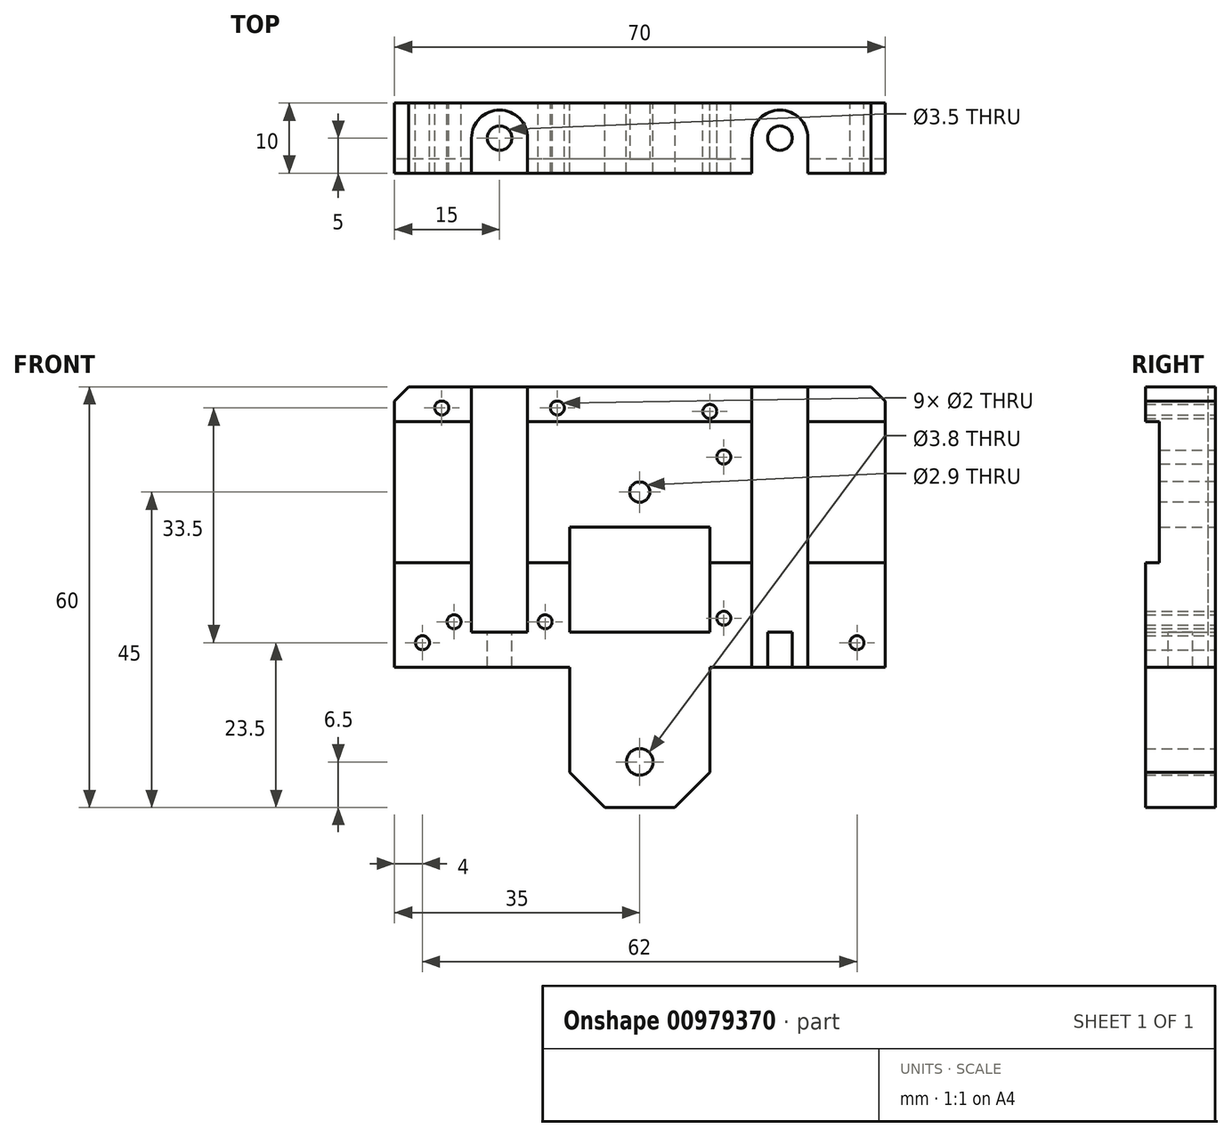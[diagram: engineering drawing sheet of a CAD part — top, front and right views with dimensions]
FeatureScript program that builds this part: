
annotation { "Feature Type Name" : "Feature", "Feature Type Description" : "" }
export const myFeature = defineFeature(function(context is Context, id is Id, definition is map)
    precondition{}
    {
        {
            var Q0;
            Q0=qCreatedBy(makeId("Front.planeOp"),FACE);
            var sketch = newSketch(context, id + "F0", { "sketchPlane" : qUnion([Q0])});
            skLineSegment(sketch, "E0.bottom", {"start": v(-35, 40) * mm, "end": v(35, 40) * mm});
            skLineSegment(sketch, "E0.top", {"start": v(-35, 0) * mm, "end": v(35, 0) * mm});
            skLineSegment(sketch, "E0.left", {"start": v(-35, 40) * mm, "end": v(-35, 0) * mm});
            skLineSegment(sketch, "E0.right", {"start": v(35, 40) * mm, "end": v(35, 0) * mm});
            skLineSegment(sketch, "E1.bottom", {"start": v(-10, -20) * mm, "end": v(10, -20) * mm});
            skLineSegment(sketch, "E1.top", {"start": v(-10, 0) * mm, "end": v(10, 0) * mm});
            skLineSegment(sketch, "E1.left", {"start": v(-10, -20) * mm, "end": v(-10, 0) * mm});
            skLineSegment(sketch, "E1.right", {"start": v(10, -20) * mm, "end": v(10, 0) * mm});
            skLineSegment(sketch, "E2", {"start": v(-20, 37) * mm, "end": v(-20, 6.5) * mm, "construction": true});
            skLineSegment(sketch, "E3", {"start": v(-28.25, 37) * mm, "end": v(-11.75, 37) * mm, "construction": true});
            skLineSegment(sketch, "E4", {"start": v(-26.5, 6.5) * mm, "end": v(-13.5, 6.5) * mm, "construction": true});
            skCircle(sketch, "E5", {"center": v(-28.25, 37) * mm, "radius": 1 * mm});
            skCircle(sketch, "E6", {"center": v(-11.75, 37) * mm, "radius": 1 * mm});
            skCircle(sketch, "E7", {"center": v(-26.5, 6.5) * mm, "radius": 1 * mm});
            skCircle(sketch, "E8", {"center": v(-13.5, 6.5) * mm, "radius": 1 * mm});
            skLineSegment(sketch, "E9.bottom", {"start": v(-10, 20) * mm, "end": v(10, 20) * mm});
            skLineSegment(sketch, "E9.top", {"start": v(-10, 5) * mm, "end": v(10, 5) * mm});
            skLineSegment(sketch, "E9.left", {"start": v(-10, 20) * mm, "end": v(-10, 5) * mm});
            skLineSegment(sketch, "E9.right", {"start": v(10, 20) * mm, "end": v(10, 5) * mm});
            skCircle(sketch, "E10", {"center": v(0, -13.5) * mm, "radius": 1.9 * mm});
            skLineSegment(sketch, "E11", {"start": v(12, 30) * mm, "end": v(12, 7) * mm, "construction": true});
            skCircle(sketch, "E12", {"center": v(12, 7) * mm, "radius": 1 * mm});
            skCircle(sketch, "E13", {"center": v(12, 30) * mm, "radius": 1 * mm});
            skLineSegment(sketch, "E14.bottom", {"start": v(31, 36.5) * mm, "end": v(-31, 36.5) * mm, "construction": true});
            skLineSegment(sketch, "E14.top", {"start": v(31, 3.5) * mm, "end": v(-31, 3.5) * mm, "construction": true});
            skLineSegment(sketch, "E14.left", {"start": v(31, 36.5) * mm, "end": v(31, 3.5) * mm, "construction": true});
            skLineSegment(sketch, "E14.right", {"start": v(-31, 36.5) * mm, "end": v(-31, 3.5) * mm, "construction": true});
            skPoint(sketch, "E15", {"position": v(-31, 20) * mm});
            skPoint(sketch, "E16", {"position": v(-35, 20) * mm});
            skCircle(sketch, "E17", {"center": v(31, 3.5) * mm, "radius": 1 * mm});
            skCircle(sketch, "E18", {"center": v(-31, 3.5) * mm, "radius": 1 * mm});
            skCircle(sketch, "E19", {"center": v(10, 36.5) * mm, "radius": 1 * mm});
            skSolve(sketch);
        }
        {
            var Q0;
            Q0=makeQuery(id+"F0.imprint","IMPRINT",FACE,{"disambiguationData":[TD([[makeQuery(id+"F0.imprint","IMPRINT",EDGE,{"derivedFrom":sQuery(id+"F0.wireOp",EDGE,"E0.bottom")}),-1.0]])]});
            var Q1;
            Q1=makeQuery(id+"F0.imprint","IMPRINT",FACE,{"disambiguationData":[TD([[makeQuery(id+"F0.imprint","IMPRINT",EDGE,{"derivedFrom":sQuery(id+"F0.wireOp",EDGE,"E1.bottom")}),1.0]])]});
            extrude(context, id + "F1", {"entities" : qUnion([Q0, Q1]), "depth" : 10 * mm, "offsetDistance" : 25 * mm});
        }
        {
            var Q0;
            Q0=makeQuery(id+"F1.opExtrude","SWEPT_FACE",FACE,{"disambiguationData":[OSD([sQuery(id+"F0.wireOp",EDGE,"E0.bottom")])]});
            var sketch = newSketch(context, id + "F2", { "sketchPlane" : qUnion([Q0])});
            skLineSegment(sketch, "E20", {"start": v(-24, -10) * mm, "end": v(-24, -5) * mm});
            skLineSegment(sketch, "E21", {"start": v(-16, -10) * mm, "end": v(-16, -5) * mm});
            skArc(sketch, "E22", {"start": v(-16, -5) * mm, "mid": v(-20, -1) * mm, "end": v(-24, -5) * mm});
            skLineSegment(sketch, "E23", {"start": v(-20, -10) * mm, "end": v(-20, 0) * mm, "construction": true});
            skLineSegment(sketch, "E24.MirrorCS", {"start": v(16, -10) * mm, "end": v(16, -5) * mm});
            skLineSegment(sketch, "E25.MirrorCS", {"start": v(24, -10) * mm, "end": v(24, -5) * mm});
            skLineSegment(sketch, "E26.MirrorCS", {"start": v(20, -10) * mm, "end": v(20, 0) * mm, "construction": true});
            skArc(sketch, "E27.MirrorCS", {"start": v(16, -5) * mm, "mid": v(20, -1) * mm, "end": v(24, -5) * mm});
            skCircle(sketch, "E28", {"center": v(-20, -5) * mm, "radius": 1.75 * mm});
            skCircle(sketch, "E29.MirrorC", {"center": v(20, -5) * mm, "radius": 1.75 * mm});
            skSolve(sketch);
        }
        {
            var Q0;
            Q0=makeQuery(id+"F2.imprint","IMPRINT",FACE,{"disambiguationData":[TD([[makeQuery(id+"F2.imprint","IMPRINT",EDGE,{"derivedFrom":sQuery(id+"F2.wireOp",EDGE,"E28")}),1.0]])]});
            var Q1;
            Q1=makeQuery(id+"F2.imprint","IMPRINT",FACE,{"disambiguationData":[TD([[makeQuery(id+"F2.imprint","IMPRINT",EDGE,{"derivedFrom":sQuery(id+"F2.wireOp",EDGE,"E29.MirrorC")}),-1.0]])]});
            extrude(context, id + "F3", {"entities" : qUnion([Q0, Q1]), "operationType" : NewBodyOperationType.REMOVE, "endBound" : BoundingType.THROUGH_ALL, "oppositeDirection" : true, "depth" : 25 * mm, "offsetDistance" : 25 * mm});
        }
        {
            var Q0;
            Q0=makeQuery(id+"F1.opExtrude","SWEPT_FACE",FACE,{"disambiguationData":[OSD([sQuery(id+"F0.wireOp",EDGE,"E0.left")])]});
            var sketch = newSketch(context, id + "F4", { "sketchPlane" : qUnion([Q0])});
            skLineSegment(sketch, "E30", {"start": v(10, 35.06) * mm, "end": v(8, 35.06) * mm});
            skLineSegment(sketch, "E31", {"start": v(8, 35.06) * mm, "end": v(8, 14.94) * mm});
            skLineSegment(sketch, "E32", {"start": v(8, 14.94) * mm, "end": v(10, 14.94) * mm});
            skPoint(sketch, "E33", {"position": v(8, 25) * mm});
            skSolve(sketch);
        }
        {
            var Q0;
            Q0 = qSketchRegion(id + "F4", true);
            var Q1;
            {var subQ0=sQuery(id+"F4.wireOp",EDGE,"E30");Q1=makeQuery(id+"F4.imprint","IMPRINT",FACE,{"disambiguationData":[TD([[makeQuery(id+"F4.imprint","IMPRINT",EDGE,{"derivedFrom":subQ0}),1.0]])]});}
            extrude(context, id + "F5", {"entities" : qUnion([Q0, Q1]), "operationType" : NewBodyOperationType.REMOVE, "endBound" : BoundingType.THROUGH_ALL, "oppositeDirection" : true, "depth" : 25 * mm, "offsetDistance" : 25 * mm});
        }
        {
            var Q0;
            Q0=makeQuery(id+"F5.boolean.opBoolean","COPY",FACE,{"disambiguationData":[TD([makeQuery(id+"F1.opExtrude","SWEPT_FACE",FACE,{"disambiguationData":[OSD([sQuery(id+"F0.wireOp",EDGE,"E9.bottom")])]})])],"derivedFrom":makeQuery(id+"F5.opExtrude","SWEPT_FACE",FACE,{"disambiguationData":[OSD([sQuery(id+"F4.wireOp",EDGE,"E31")])]})});
            var sketch = newSketch(context, id + "F6", { "sketchPlane" : qUnion([Q0])});
            skCircle(sketch, "E34", {"center": v(0, 25) * mm, "radius": 1.45 * mm});
            skLineSegment(sketch, "E35", {"start": v(-35, 25) * mm, "end": v(35, 25) * mm, "construction": true});
            skSolve(sketch);
        }
        {
            var Q0;
            Q0=makeQuery(id+"F6.imprint","IMPRINT",FACE,{"disambiguationData":[TD([[makeQuery(id+"F6.imprint","IMPRINT",EDGE,{"derivedFrom":sQuery(id+"F6.wireOp",EDGE,"E34")}),1.0]])]});
            extrude(context, id + "F7", {"entities" : qUnion([Q0]), "operationType" : NewBodyOperationType.REMOVE, "endBound" : BoundingType.THROUGH_ALL, "oppositeDirection" : true, "depth" : 25 * mm, "offsetDistance" : 25 * mm});
        }
        {
            var Q0;
            Q0 = qSketchRegion(id + "F2", true);
            var Q1;
            {var subQ0=sQuery(id+"F2.wireOp",EDGE,"E20");Q1=makeQuery(id+"F2.imprint","IMPRINT",FACE,{"disambiguationData":[TD([[makeQuery(id+"F2.imprint","IMPRINT",EDGE,{"derivedFrom":subQ0}),-1.0]])]});}
            var Q2;
            {var subQ1=sQuery(id+"F2.wireOp",EDGE,"E24.MirrorCS");Q2=makeQuery(id+"F2.imprint","IMPRINT",FACE,{"disambiguationData":[TD([[makeQuery(id+"F2.imprint","IMPRINT",EDGE,{"derivedFrom":subQ1}),-1.0]])]});}
            extrude(context, id + "F8", {"entities" : qUnion([Q0, Q1, Q2]), "operationType" : NewBodyOperationType.REMOVE, "oppositeDirection" : true, "depth" : 35 * mm, "offsetDistance" : 25 * mm});
        }
        {
            var Q0;
            Q0=makeQuery(id+"F1.opExtrude","SWEPT_EDGE",EDGE,{"disambiguationData":[OSD([sQuery(id+"F0.wireOp",EDGE,"E1.bottom"),sQuery(id+"F0.wireOp",EDGE,"E1.right")])]});
            var Q1;
            Q1=makeQuery(id+"F1.opExtrude","SWEPT_EDGE",EDGE,{"disambiguationData":[OSD([sQuery(id+"F0.wireOp",EDGE,"E1.bottom"),sQuery(id+"F0.wireOp",EDGE,"E1.left")])]});
            chamfer(context, id + "F9", {"entities" : qUnion([Q0, Q1]), "width" : 5 * mm, "tangentPropagation" : true});
        }
        {
            var Q0;
            Q0=makeQuery(id+"F1.opExtrude","SWEPT_EDGE",EDGE,{"disambiguationData":[OSD([sQuery(id+"F0.wireOp",EDGE,"E0.bottom"),sQuery(id+"F0.wireOp",EDGE,"E0.left")])]});
            var Q1;
            Q1=makeQuery(id+"F1.opExtrude","SWEPT_EDGE",EDGE,{"disambiguationData":[OSD([sQuery(id+"F0.wireOp",EDGE,"E0.bottom"),sQuery(id+"F0.wireOp",EDGE,"E0.right")])]});
            chamfer(context, id + "F10", {"entities" : qUnion([Q0, Q1]), "width" : 2 * mm, "tangentPropagation" : true});
        }
    });
